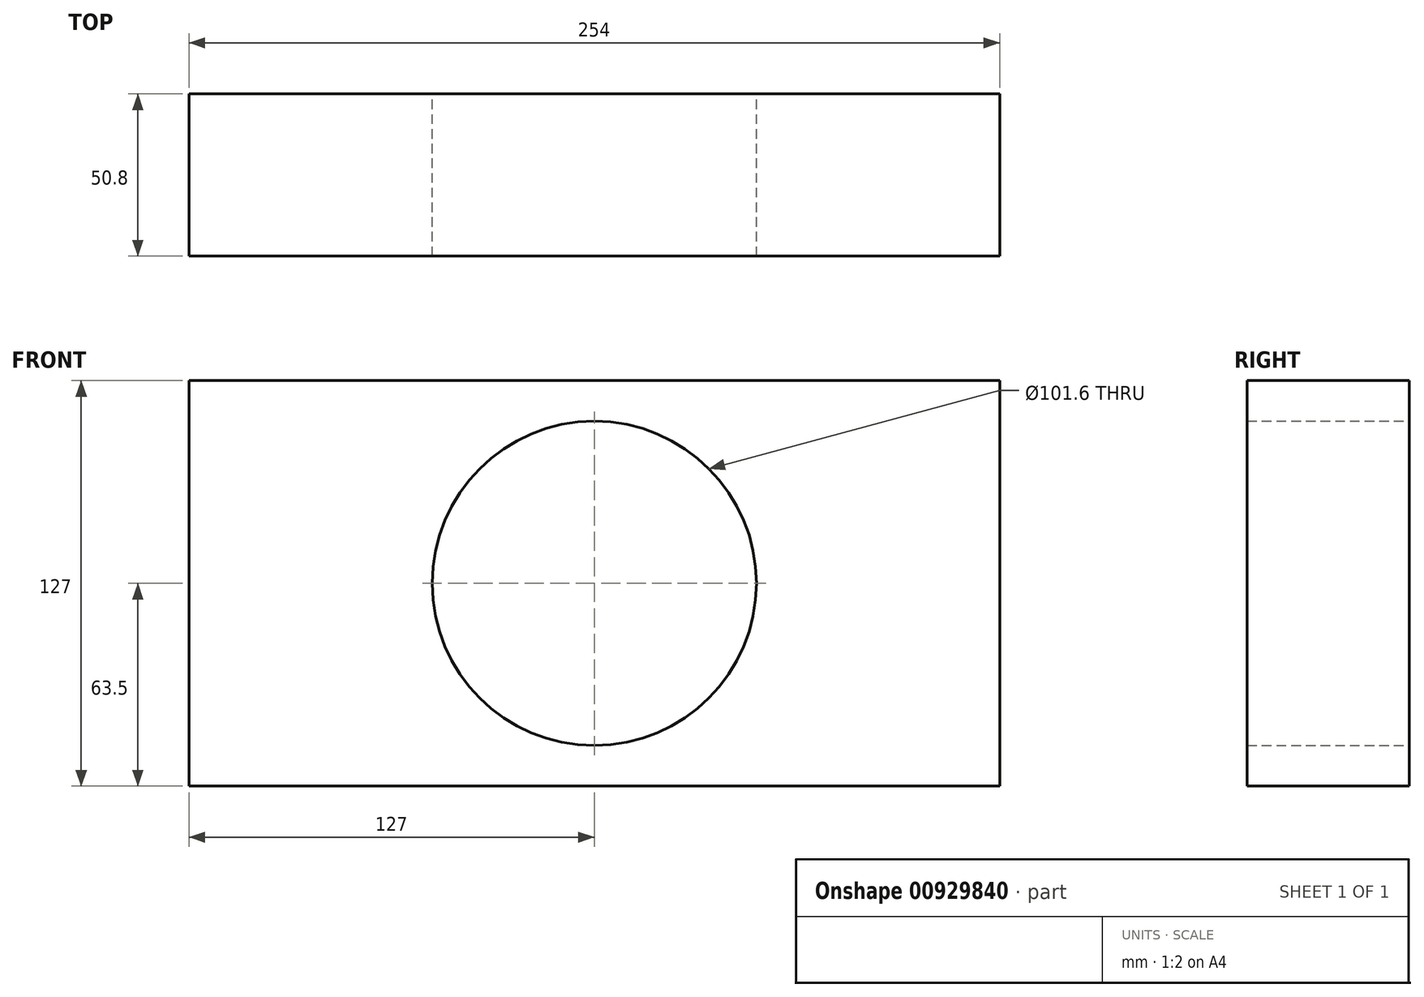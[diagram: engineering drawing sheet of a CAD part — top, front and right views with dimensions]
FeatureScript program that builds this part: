
annotation { "Feature Type Name" : "Feature", "Feature Type Description" : "" }
export const myFeature = defineFeature(function(context is Context, id is Id, definition is map)
    precondition{}
    {
        {
            var Q0;
            Q0=qCreatedBy(makeId("Front.planeOp"),FACE);
            var sketch = newSketch(context, id + "F0", { "sketchPlane" : qUnion([Q0])});
            skLineSegment(sketch, "E0", {"start": v(0, 0) * mm, "end": v(254, 0) * mm});
            skLineSegment(sketch, "E1", {"start": v(254, 0) * mm, "end": v(254, 127) * mm});
            skLineSegment(sketch, "E2", {"start": v(254, 127) * mm, "end": v(0, 127) * mm});
            skLineSegment(sketch, "E3", {"start": v(0, 127) * mm, "end": v(0, 0) * mm});
            skCircle(sketch, "E4", {"center": v(127, 63.5) * mm, "radius": 50.8 * mm});
            skLineSegment(sketch, "E5", {"start": v(127, 63.5) * mm, "end": v(127, 0) * mm, "construction": true});
            skLineSegment(sketch, "E6", {"start": v(127, 63.5) * mm, "end": v(127, 127) * mm, "construction": true});
            skSolve(sketch);
        }
        {
            var Q0;
            Q0 = qSketchRegion(id + "F0", true);
            extrude(context, id + "F1", {"entities" : qUnion([Q0]), "depth" : 50.8 * mm, "offsetDistance" : 25.4 * mm});
        }
    });
